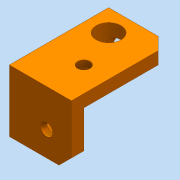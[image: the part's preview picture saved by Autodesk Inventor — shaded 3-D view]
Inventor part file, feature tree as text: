
AUTODESK INVENTOR PART (.ipt)
format: ipt  version: 2016 (Build 200138000, 138)  size: 128,000 bytes
history: native  units: mm (DEFAULTED — no unit token found)
features: sketch x5, other x3
ambient origin geometry x8: Origin, YZ Plane, XZ Plane, XY Plane, X Axis, Y Axis, Z Axis, Center Point
bodies: Solid1 (feature_tree)
feature tree (8):
  other  "Frame3WayBlockMotor.ipt"
  other  "Solid1::Frame3WayBlockMotor.ipt"
  other  "TaggingFeature1"
  sketch  "Sketch1"  dims[d0=10.0mm]
  sketch  "Sketch2"
  sketch  "Sketch3"
  sketch  "Sketch4"
  sketch  "Sketch5"
